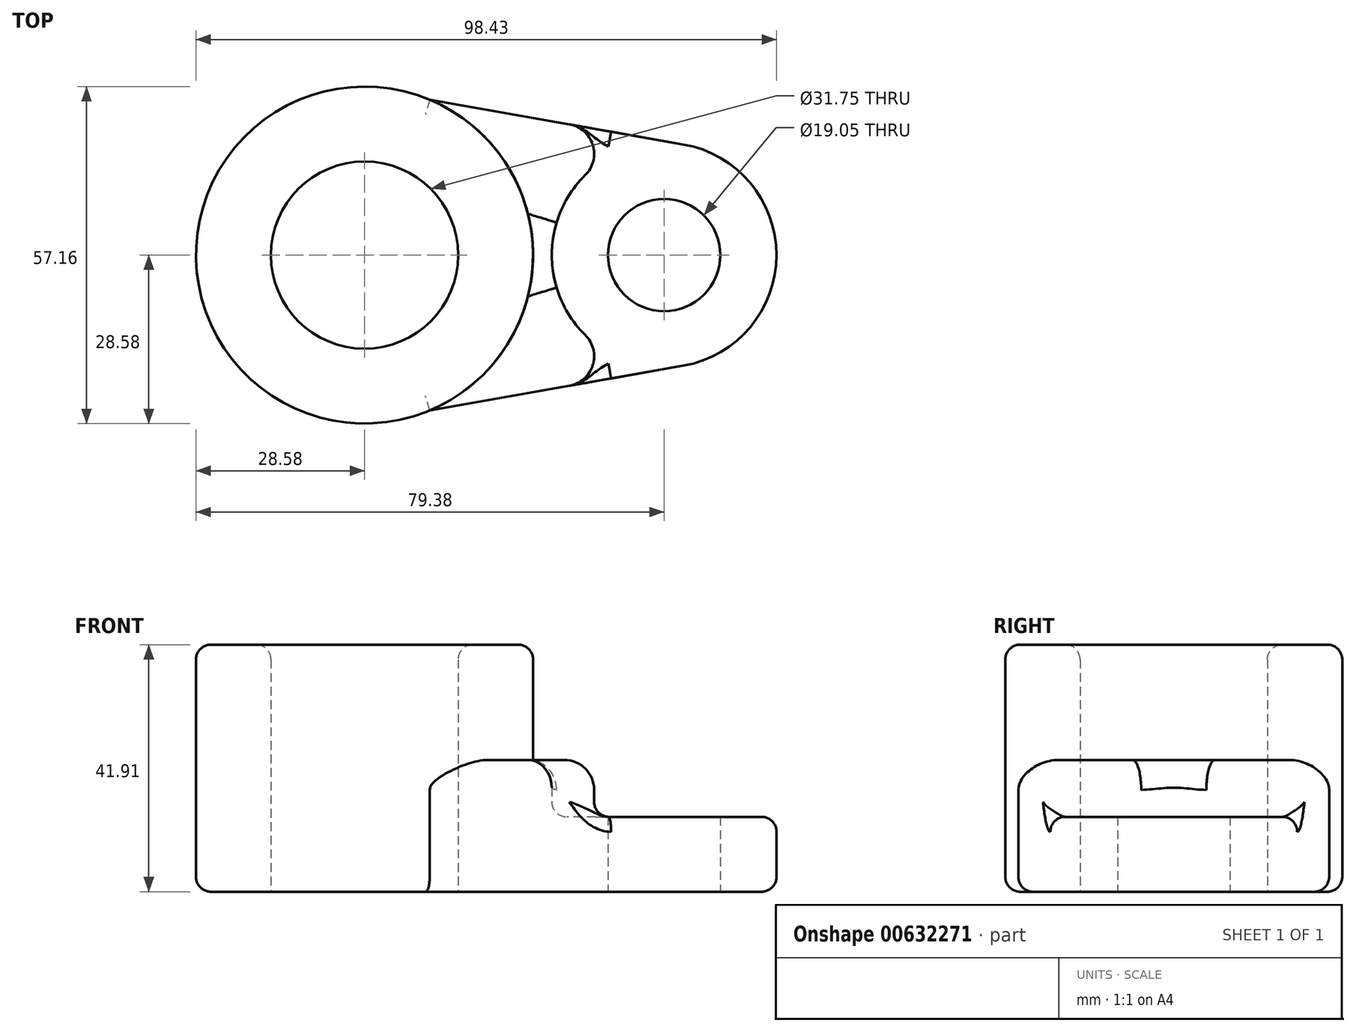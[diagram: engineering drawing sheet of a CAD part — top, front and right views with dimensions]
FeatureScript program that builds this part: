
annotation { "Feature Type Name" : "Feature", "Feature Type Description" : "" }
export const myFeature = defineFeature(function(context is Context, id is Id, definition is map)
    precondition{}
    {
        {
            var Q0;
            Q0=qCreatedBy(makeId("Top.planeOp"),FACE);
            var sketch = newSketch(context, id + "F0", { "sketchPlane" : qUnion([Q0])});
            skCircle(sketch, "E0", {"center": v(0, 0) * mm, "radius": 28.58 * mm});
            skCircle(sketch, "E1", {"center": v(0, 0) * mm, "radius": 15.88 * mm});
            skCircle(sketch, "E2", {"center": v(50.8, 0) * mm, "radius": 19.05 * mm});
            skCircle(sketch, "E3", {"center": v(50.8, 0) * mm, "radius": 9.53 * mm});
            skLineSegment(sketch, "E4", {"start": v(11.06, 26.35) * mm, "end": v(54.1, 18.76) * mm});
            skLineSegment(sketch, "E5", {"start": v(11.06, -26.35) * mm, "end": v(54.1, -18.76) * mm});
            skSolve(sketch);
        }
        {
            var Q0;
            Q0=makeQuery(id+"F0.imprint","IMPRINT",FACE,{"disambiguationData":[TD([[makeQuery(id+"F0.imprint","IMPRINT",EDGE,{"derivedFrom":sQuery(id+"F0.wireOp",EDGE,"E1")}),-1.0]])]});
            extrude(context, id + "F1", {"entities" : qUnion([Q0]), "depth" : 41.9 * mm, "offsetDistance" : 25.4 * mm});
        }
        {
            var Q0;
            {var subQ0=sQuery(id+"F0.wireOp",EDGE,"E4");Q0=makeQuery(id+"F0.imprint","IMPRINT",FACE,{"disambiguationData":[TD([[makeQuery(id+"F0.imprint","IMPRINT",EDGE,{"derivedFrom":subQ0}),-1.0]])]});}
            extrude(context, id + "F2", {"entities" : qUnion([Q0]), "operationType" : NewBodyOperationType.ADD, "depth" : 22.35 * mm, "offsetDistance" : 25.4 * mm});
        }
        {
            var Q0;
            Q0=makeQuery(id+"F0.imprint","IMPRINT",FACE,{"disambiguationData":[TD([[makeQuery(id+"F0.imprint","IMPRINT",EDGE,{"derivedFrom":sQuery(id+"F0.wireOp",EDGE,"E3")}),-1.0]])]});
            extrude(context, id + "F3", {"entities" : qUnion([Q0]), "operationType" : NewBodyOperationType.ADD, "depth" : 12.7 * mm, "offsetDistance" : 25.4 * mm});
        }
        {
            var Q0;
            {var subQ0=sQuery(id+"F0.wireOp",EDGE,"E2");var subQ1=sQuery(id+"F0.wireOp",EDGE,"E5");Q0=makeQuery(id+"F3.boolean.opBoolean","SPLIT",EDGE,{"disambiguationData":[topologyDisambiguationEdgeConnected([makeQuery(id+"F2.opExtrude","SWEPT_FACE",FACE,{"disambiguationData":[OSD([subQ0])]})])],"derivedFrom":makeQuery(id+"F2.opExtrude","SWEPT_EDGE",EDGE,{"disambiguationData":[OSD([subQ0,subQ1])]})});}
            fillet(context, id + "F4", {"entities" : qUnion([Q0]), "radius" : 5.08 * mm, "tangentPropagation" : true, "allowEdgeOverflow" : false});
        }
        {
            var Q0;
            {var subQ0=sQuery(id+"F0.wireOp",EDGE,"E2");var subQ1=sQuery(id+"F0.wireOp",EDGE,"E4");Q0=makeQuery(id+"F3.boolean.opBoolean","SPLIT",EDGE,{"disambiguationData":[topologyDisambiguationEdgeConnected([makeQuery(id+"F2.opExtrude","SWEPT_FACE",FACE,{"disambiguationData":[OSD([subQ0])]})])],"derivedFrom":makeQuery(id+"F2.opExtrude","SWEPT_EDGE",EDGE,{"disambiguationData":[OSD([subQ0,subQ1])]})});}
            fillet(context, id + "F5", {"entities" : qUnion([Q0]), "radius" : 5.08 * mm, "tangentPropagation" : true, "allowEdgeOverflow" : false});
        }
        {
            var Q0;
            {var subQ0=sQuery(id+"F0.wireOp",EDGE,"E2");Q0=makeQuery(id+"F4.opFillet","TWEAK_EDGE",EDGE,{"derivedFrom":[makeQuery(id+"F3.boolean.opBoolean","TWEAK_VERTEX",VERTEX,{"derivedFrom":[makeQuery(id+"F2.opExtrude","SWEPT_FACE",FACE,{"disambiguationData":[OSD([subQ0])]}),makeQuery(id+"F2.opExtrude","SWEPT_FACE",FACE,{"disambiguationData":[OSD([sQuery(id+"F0.wireOp",EDGE,"E5")])]}),makeQuery(id+"F3.opExtrude","SWEPT_FACE",FACE,{"disambiguationData":[OSD([subQ0])]}),makeQuery(id+"F3.opExtrude","CAP_FACE",FACE,{"disambiguationData":[OSD([subQ0,sQuery(id+"F0.wireOp",EDGE,"E3")])],"isStart":false})]})]});}
            var Q1;
            {var subQ0=sQuery(id+"F0.wireOp",EDGE,"E2");Q1=makeQuery(id+"F3.boolean.opBoolean","SPLIT",EDGE,{"disambiguationData":[topologyDisambiguationEdgeConnected([makeQuery(id+"F3.opExtrude","SWEPT_FACE",FACE,{"disambiguationData":[OSD([subQ0])]})])],"derivedFrom":makeQuery(id+"F3.opExtrude","CAP_EDGE",EDGE,{"disambiguationData":[OSD([subQ0])],"isStart":false})});}
            var Q2;
            {var subQ0=sQuery(id+"F0.wireOp",EDGE,"E2");Q2=makeQuery(id+"F5.opFillet","TWEAK_EDGE",EDGE,{"derivedFrom":[makeQuery(id+"F3.boolean.opBoolean","TWEAK_VERTEX",VERTEX,{"derivedFrom":[makeQuery(id+"F2.opExtrude","SWEPT_FACE",FACE,{"disambiguationData":[OSD([subQ0])]}),makeQuery(id+"F2.opExtrude","SWEPT_FACE",FACE,{"disambiguationData":[OSD([sQuery(id+"F0.wireOp",EDGE,"E4")])]}),makeQuery(id+"F3.opExtrude","SWEPT_FACE",FACE,{"disambiguationData":[OSD([subQ0])]}),makeQuery(id+"F3.opExtrude","CAP_FACE",FACE,{"disambiguationData":[OSD([subQ0,sQuery(id+"F0.wireOp",EDGE,"E3")])],"isStart":false})]})]});}
            var Q3;
            {var subQ0=sQuery(id+"F0.wireOp",EDGE,"E2");var subQ1=sQuery(id+"F0.wireOp",EDGE,"E4");Q3=makeQuery(id+"F5.opFillet","BLEND_EDGE",EDGE,{"blendedFrom":[makeQuery(id+"F3.boolean.opBoolean","SPLIT",EDGE,{"disambiguationData":[topologyDisambiguationEdgeConnected([makeQuery(id+"F2.opExtrude","SWEPT_FACE",FACE,{"disambiguationData":[OSD([subQ0])]})])],"derivedFrom":makeQuery(id+"F2.opExtrude","SWEPT_EDGE",EDGE,{"disambiguationData":[OSD([subQ0,subQ1])]})}),makeQuery(id+"F3.opExtrude","CAP_FACE",FACE,{"disambiguationData":[OSD([subQ0,sQuery(id+"F0.wireOp",EDGE,"E3")])],"isStart":false})],"blendedInto":[makeQuery(id+"F3.opExtrude","CAP_FACE",FACE,{"disambiguationData":[OSD([subQ0,sQuery(id+"F0.wireOp",EDGE,"E3")])],"isStart":false})]});}
            var Q4;
            {var subQ0=sQuery(id+"F0.wireOp",EDGE,"E2");Q4=makeQuery(id+"F3.boolean.opBoolean","SPLIT",EDGE,{"disambiguationData":[topologyDisambiguationEdgeConnected([makeQuery(id+"F2.opExtrude","SWEPT_FACE",FACE,{"disambiguationData":[OSD([subQ0])]})])],"derivedFrom":makeQuery(id+"F3.opExtrude","CAP_EDGE",EDGE,{"disambiguationData":[OSD([subQ0])],"isStart":false})});}
            var Q5;
            {var subQ0=sQuery(id+"F0.wireOp",EDGE,"E2");var subQ1=sQuery(id+"F0.wireOp",EDGE,"E5");Q5=makeQuery(id+"F4.opFillet","BLEND_EDGE",EDGE,{"blendedFrom":[makeQuery(id+"F3.boolean.opBoolean","SPLIT",EDGE,{"disambiguationData":[topologyDisambiguationEdgeConnected([makeQuery(id+"F2.opExtrude","SWEPT_FACE",FACE,{"disambiguationData":[OSD([subQ0])]})])],"derivedFrom":makeQuery(id+"F2.opExtrude","SWEPT_EDGE",EDGE,{"disambiguationData":[OSD([subQ0,subQ1])]})}),makeQuery(id+"F3.opExtrude","CAP_FACE",FACE,{"disambiguationData":[OSD([subQ0,sQuery(id+"F0.wireOp",EDGE,"E3")])],"isStart":false})],"blendedInto":[makeQuery(id+"F3.opExtrude","CAP_FACE",FACE,{"disambiguationData":[OSD([subQ0,sQuery(id+"F0.wireOp",EDGE,"E3")])],"isStart":false})]});}
            fillet(context, id + "F6", {"entities" : qUnion([Q0, Q1, Q2, Q3, Q4, Q5]), "radius" : 2.54 * mm, "tangentPropagation" : true, "allowEdgeOverflow" : false});
        }
        {
            var Q0;
            Q0=makeQuery(id+"F1.opExtrude","CAP_EDGE",EDGE,{"disambiguationData":[OSD([sQuery(id+"F0.wireOp",EDGE,"E0")])],"isStart":false});
            var Q1;
            Q1=makeQuery(id+"F1.opExtrude","CAP_EDGE",EDGE,{"disambiguationData":[OSD([sQuery(id+"F0.wireOp",EDGE,"E1")])],"isStart":false});
            fillet(context, id + "F7", {"entities" : qUnion([Q0, Q1]), "radius" : 2.54 * mm, "tangentPropagation" : true, "allowEdgeOverflow" : false});
        }
        {
            var Q0;
            {var subQ0=sQuery(id+"F0.wireOp",EDGE,"E5");var subQ1=sQuery(id+"F0.wireOp",EDGE,"E2");Q0=makeQuery(id+"F4.opFillet","BLEND_EDGE",EDGE,{"blendedFrom":[makeQuery(id+"F3.boolean.opBoolean","SPLIT",EDGE,{"disambiguationData":[topologyDisambiguationEdgeConnected([makeQuery(id+"F2.opExtrude","SWEPT_FACE",FACE,{"disambiguationData":[OSD([subQ1])]})])],"derivedFrom":makeQuery(id+"F2.opExtrude","SWEPT_EDGE",EDGE,{"disambiguationData":[OSD([subQ1,subQ0])]})}),makeQuery(id+"F2.opExtrude","CAP_FACE",FACE,{"disambiguationData":[OSD([sQuery(id+"F0.wireOp",EDGE,"E0"),subQ1,sQuery(id+"F0.wireOp",EDGE,"E4"),subQ0])],"isStart":false})],"blendedInto":[makeQuery(id+"F2.opExtrude","CAP_FACE",FACE,{"disambiguationData":[OSD([sQuery(id+"F0.wireOp",EDGE,"E0"),subQ1,sQuery(id+"F0.wireOp",EDGE,"E4"),subQ0])],"isStart":false})]});}
            var Q1;
            {var subQ0=sQuery(id+"F0.wireOp",EDGE,"E4");var subQ1=sQuery(id+"F0.wireOp",EDGE,"E2");Q1=makeQuery(id+"F5.opFillet","BLEND_EDGE",EDGE,{"blendedFrom":[makeQuery(id+"F3.boolean.opBoolean","SPLIT",EDGE,{"disambiguationData":[topologyDisambiguationEdgeConnected([makeQuery(id+"F2.opExtrude","SWEPT_FACE",FACE,{"disambiguationData":[OSD([subQ1])]})])],"derivedFrom":makeQuery(id+"F2.opExtrude","SWEPT_EDGE",EDGE,{"disambiguationData":[OSD([subQ1,subQ0])]})}),makeQuery(id+"F2.opExtrude","CAP_FACE",FACE,{"disambiguationData":[OSD([sQuery(id+"F0.wireOp",EDGE,"E0"),subQ1,subQ0,sQuery(id+"F0.wireOp",EDGE,"E5")])],"isStart":false})],"blendedInto":[makeQuery(id+"F2.opExtrude","CAP_FACE",FACE,{"disambiguationData":[OSD([sQuery(id+"F0.wireOp",EDGE,"E0"),subQ1,subQ0,sQuery(id+"F0.wireOp",EDGE,"E5")])],"isStart":false})]});}
            fillet(context, id + "F8", {"entities" : qUnion([Q0, Q1]), "radius" : 5.08 * mm, "tangentPropagation" : true, "allowEdgeOverflow" : false});
        }
        {
            var Q0;
            Q0=makeQuery(id+"F2.opExtrude","CAP_EDGE",EDGE,{"disambiguationData":[OSD([sQuery(id+"F0.wireOp",EDGE,"E5")])],"isStart":true});
            var Q1;
            Q1=makeQuery(id+"F1.opExtrude","CAP_EDGE",EDGE,{"disambiguationData":[OSD([sQuery(id+"F0.wireOp",EDGE,"E0")])],"isStart":true});
            var Q2;
            Q2=makeQuery(id+"F2.opExtrude","CAP_EDGE",EDGE,{"disambiguationData":[OSD([sQuery(id+"F0.wireOp",EDGE,"E4")])],"isStart":true});
            var Q3;
            Q3=makeQuery(id+"F3.opExtrude","CAP_EDGE",EDGE,{"disambiguationData":[OSD([sQuery(id+"F0.wireOp",EDGE,"E2")])],"isStart":true});
            fillet(context, id + "F9", {"entities" : qUnion([Q0, Q1, Q2, Q3]), "radius" : 2.54 * mm, "tangentPropagation" : true, "allowEdgeOverflow" : false});
        }
    });
